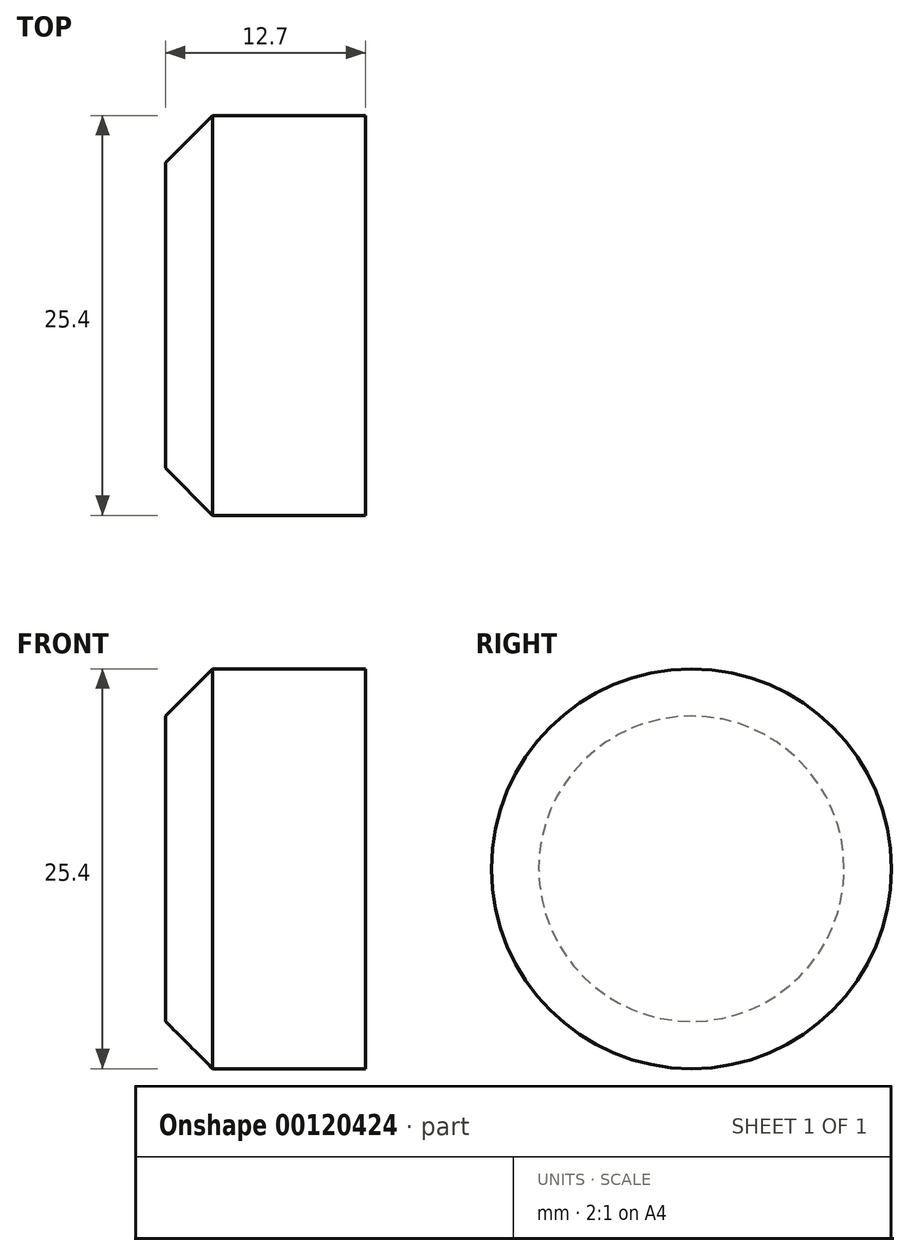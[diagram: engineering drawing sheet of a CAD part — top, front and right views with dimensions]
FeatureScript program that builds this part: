
annotation { "Feature Type Name" : "Feature", "Feature Type Description" : "" }
export const myFeature = defineFeature(function(context is Context, id is Id, definition is map)
    precondition{}
    {
        {
            var Q0;
            Q0=qCreatedBy(makeId("Front.planeOp"),FACE);
            var sketch = newSketch(context, id + "F0", { "sketchPlane" : qUnion([Q0])});
            skLineSegment(sketch, "E0", {"start": v(0, 0) * mm, "end": v(0, 12.7) * mm});
            skLineSegment(sketch, "E1", {"start": v(0, 12.7) * mm, "end": v(12.7, 12.7) * mm});
            skLineSegment(sketch, "E2", {"start": v(12.7, 12.7) * mm, "end": v(12.7, 0) * mm});
            skLineSegment(sketch, "E3", {"start": v(12.7, 0) * mm, "end": v(0, 0) * mm});
            skSolve(sketch);
        }
        {
            var Q0;
            Q0=makeQuery(id+"F0.imprint","IMPRINT",FACE,{"disambiguationData":[TD([[makeQuery(id+"F0.imprint","IMPRINT",EDGE,{"derivedFrom":sQuery(id+"F0.wireOp",EDGE,"E0")}),-1.0]])]});
            var Q1;
            Q1=sQuery(id+"F0.wireOp",EDGE,"E3");
            revolve(context, id + "F1", {"entities" : qUnion([Q0]), "axis" : qUnion([Q1]), "revolveType" : RevolveType.FULL});
        }
        {
            var Q0;
            Q0=makeQuery(id+"F1.opRevolve","SWEPT_EDGE",EDGE,{"disambiguationData":[OSD([sQuery(id+"F0.wireOp",EDGE,"E0"),sQuery(id+"F0.wireOp",EDGE,"E1")])]});
            chamfer(context, id + "F2", {"entities" : qUnion([Q0]), "width" : 3 * mm, "tangentPropagation" : true});
        }
    });
